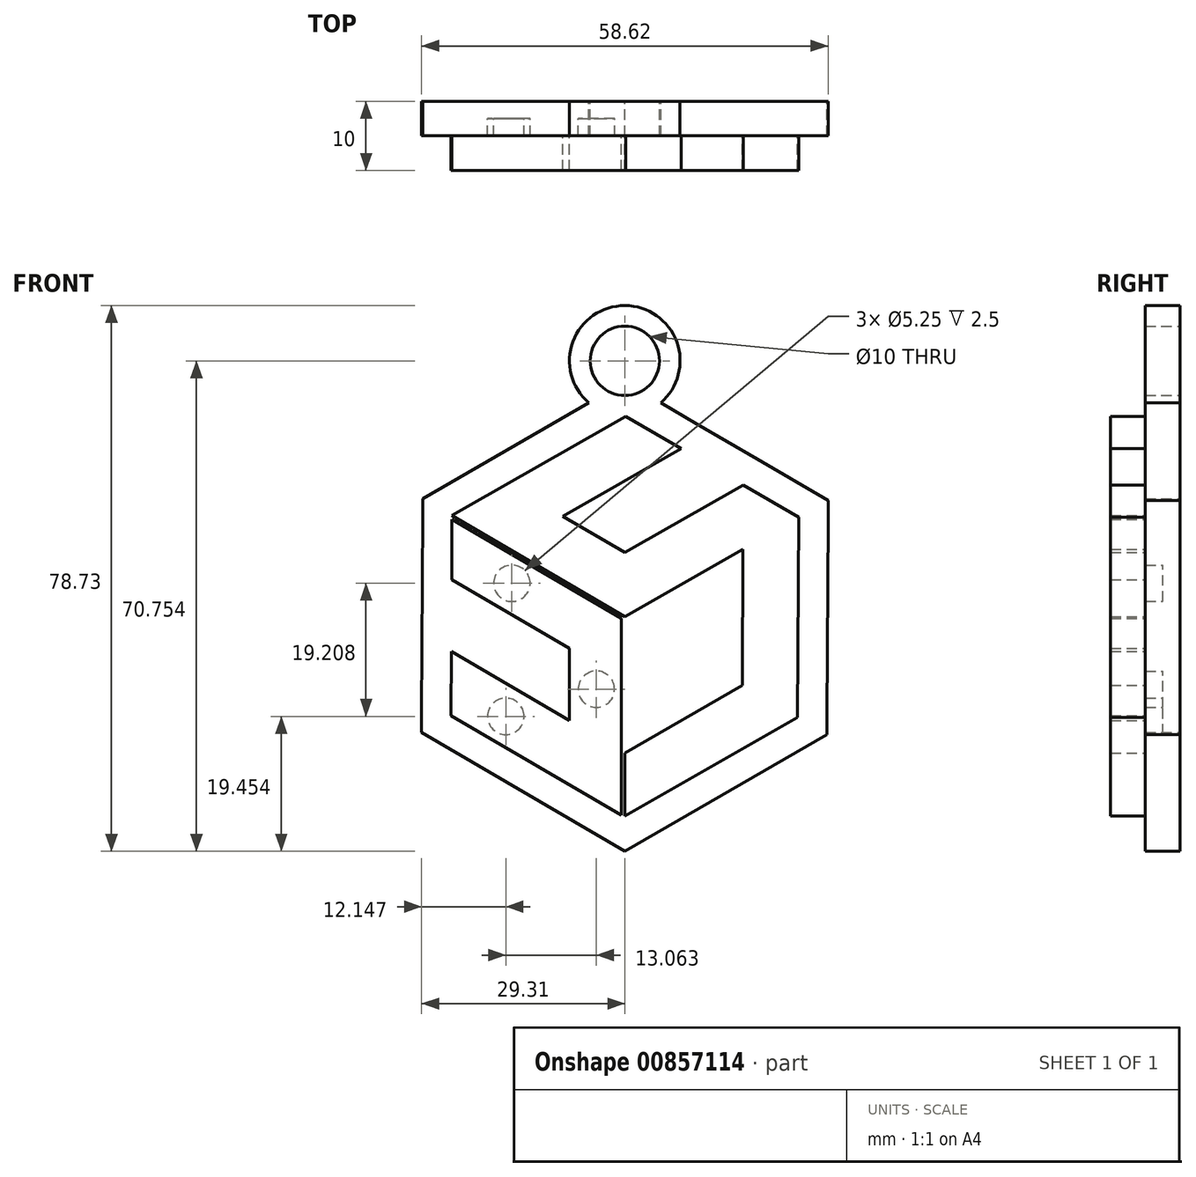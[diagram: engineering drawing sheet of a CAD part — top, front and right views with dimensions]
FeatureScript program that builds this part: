
annotation { "Feature Type Name" : "Feature", "Feature Type Description" : "" }
export const myFeature = defineFeature(function(context is Context, id is Id, definition is map)
    precondition{}
    {
        {
            var Q0;
            Q0=qCreatedBy(makeId("Front.planeOp"),FACE);
            var sketch = newSketch(context, id + "F0", { "sketchPlane" : qUnion([Q0])});
            skCircle(sketch, "E0.cCircle", {"center": v(0, 0) * mm, "radius": 25 * mm, "construction": true});
            skLineSegment(sketch, "E0.0", {"start": v(24.92, -14.56) * mm, "end": v(0, -28.78) * mm});
            skLineSegment(sketch, "E0.3", {"start": v(-24.92, 14.56) * mm, "end": v(0.15, 28.87) * mm});
            skLineSegment(sketch, "E0.5", {"start": v(25.07, 14.3) * mm, "end": v(24.92, -14.56) * mm});
            skPoint(sketch, "E0.0.midPoint", {"position": v(12.39, -21.72) * mm});
            skLineSegment(sketch, "E1.0", {"start": v(-8.93, 14.48) * mm, "end": v(8.13, 24.2) * mm});
            skLineSegment(sketch, "E2.0", {"start": v(17.1, 18.96) * mm, "end": v(0, 9.27) * mm});
            skLineSegment(sketch, "E3.0", {"start": v(-8.93, 14.48) * mm, "end": v(0, 9.27) * mm});
            skLineSegment(sketch, "E4.0", {"start": v(17.05, 9.73) * mm, "end": v(16.95, -9.9) * mm});
            skLineSegment(sketch, "E5", {"start": v(16.95, -9.9) * mm, "end": v(0, -19.69) * mm});
            skLineSegment(sketch, "E6", {"start": v(17.05, 9.73) * mm, "end": v(0, 0) * mm});
            skLineSegment(sketch, "E7", {"start": v(0, 0) * mm, "end": v(-24.92, 14.56) * mm});
            skLineSegment(sketch, "E8", {"start": v(0.15, 28.87) * mm, "end": v(8.13, 24.2) * mm});
            skLineSegment(sketch, "E9", {"start": v(17.1, 18.96) * mm, "end": v(25.07, 14.3) * mm});
            skLineSegment(sketch, "E10", {"start": v(0, -19.69) * mm, "end": v(0, -28.78) * mm});
            skLineSegment(sketch, "E11", {"start": v(0, -28.78) * mm, "end": v(0, -28.78) * mm});
            skSolve(sketch);
        }
        {
            var Q0;
            Q0 = qSketchRegion(id + "F0", true);
            extrude(context, id + "F1", {"entities" : qUnion([Q0]), "depth" : 10 * mm, "offsetDistance" : 25 * mm});
        }
        {
            var Q0;
            Q0=qCreatedBy(makeId("Front.planeOp"),FACE);
            var sketch = newSketch(context, id + "F2", { "sketchPlane" : qUnion([Q0])});
            skLineSegment(sketch, "E12.0", {"start": v(19.12, 22.7) * mm, "end": v(29.31, 16.74) * mm});
            skLineSegment(sketch, "E13.0", {"start": v(29.31, 13.92) * mm, "end": v(29.16, -14.22) * mm});
            skLineSegment(sketch, "E14.0", {"start": v(0, -33.86) * mm, "end": v(-29.31, -16.74) * mm});
            skLineSegment(sketch, "E15.0", {"start": v(-29.26, -4.91) * mm, "end": v(-29.31, -13.92) * mm});
            skLineSegment(sketch, "E16.0", {"start": v(-29.16, 14.66) * mm, "end": v(-29.21, 5.22) * mm});
            skLineSegment(sketch, "E17", {"start": v(-29.16, 17.02) * mm, "end": v(-29.16, 14.66) * mm});
            skLineSegment(sketch, "E18", {"start": v(-29.21, 5.22) * mm, "end": v(-29.26, -4.91) * mm});
            skLineSegment(sketch, "E19", {"start": v(-29.31, -13.92) * mm, "end": v(-29.31, -16.74) * mm});
            skLineSegment(sketch, "E20", {"start": v(29.16, -14.22) * mm, "end": v(29.16, -17.02) * mm});
            skLineSegment(sketch, "E21", {"start": v(10.38, 27.8) * mm, "end": v(19.12, 22.7) * mm});
            skLineSegment(sketch, "E22", {"start": v(29.31, 16.74) * mm, "end": v(29.31, 13.92) * mm});
            skLineSegment(sketch, "E23", {"start": v(-29.16, 17.02) * mm, "end": v(-6.93, 29.86) * mm});
            skLineSegment(sketch, "E24", {"start": v(0, -33.86) * mm, "end": v(29.16, -17.02) * mm});
            skLineSegment(sketch, "E25", {"start": v(6.9, 29.83) * mm, "end": v(10.38, 27.8) * mm});
            skLineSegment(sketch, "E26", {"start": v(-6.93, 29.86) * mm, "end": v(-5.2, 30.86) * mm});
            skLineSegment(sketch, "E27", {"start": v(6.9, 29.83) * mm, "end": v(5.18, 30.83) * mm});
            skPoint(sketch, "E28", {"position": v(0, 36.9) * mm});
            skArc(sketch, "E29", {"start": v(5.18, 30.83) * mm, "mid": v(0.02, 44.87) * mm, "end": v(-5.2, 30.86) * mm});
            skSolve(sketch);
        }
        {
            var Q0;
            Q0 = qSketchRegion(id + "F2", true);
            extrude(context, id + "F3", {"entities" : qUnion([Q0]), "operationType" : NewBodyOperationType.ADD, "depth" : 5 * mm, "offsetDistance" : 25 * mm});
        }
        {
            var Q0;
            Q0=qCreatedBy(makeId("Front.planeOp"),FACE);
            var sketch = newSketch(context, id + "F4", { "sketchPlane" : qUnion([Q0])});
            skLineSegment(sketch, "E30.0", {"start": v(-8, -4.6) * mm, "end": v(-24.97, 5.33) * mm});
            skLineSegment(sketch, "E31.0", {"start": v(-8, -4.6) * mm, "end": v(-8, -15.01) * mm});
            skLineSegment(sketch, "E32.0", {"start": v(-25.03, -5.07) * mm, "end": v(-8, -15.01) * mm});
            skLineSegment(sketch, "E33.0", {"start": v(-25.03, -5.07) * mm, "end": v(-25.07, -14.3) * mm});
            skLineSegment(sketch, "E34.0", {"start": v(-0.5, -19.69) * mm, "end": v(-0.5, -28.66) * mm});
            skLineSegment(sketch, "E35", {"start": v(-0.5, -0.29) * mm, "end": v(-24.93, 13.99) * mm});
            skLineSegment(sketch, "E36", {"start": v(-0.5, -0.29) * mm, "end": v(-0.5, -19.69) * mm});
            skLineSegment(sketch, "E37", {"start": v(-0.5, -28.66) * mm, "end": v(-25.07, -14.3) * mm});
            skLineSegment(sketch, "E38", {"start": v(-24.93, 13.99) * mm, "end": v(-24.97, 5.33) * mm});
            skSolve(sketch);
        }
        {
            var Q0;
            Q0=sQuery(id+"F2.wireOp",VERTEX,"E28");
            var Q1;
            Q1=makeQuery(id+"F1.opExtrude","SWEPT_BODY",BODY,{"disambiguationData":[OSD([sQuery(id+"F0.wireOp",EDGE,"E0.0"),sQuery(id+"F0.wireOp",EDGE,"E0.3"),sQuery(id+"F0.wireOp",EDGE,"E0.5"),sQuery(id+"F0.wireOp",EDGE,"E1.0"),sQuery(id+"F0.wireOp",EDGE,"E2.0"),sQuery(id+"F0.wireOp",EDGE,"E3.0"),sQuery(id+"F0.wireOp",EDGE,"E4.0"),sQuery(id+"F0.wireOp",EDGE,"E5"),sQuery(id+"F0.wireOp",EDGE,"E6"),sQuery(id+"F0.wireOp",EDGE,"E7"),sQuery(id+"F0.wireOp",EDGE,"E8"),sQuery(id+"F0.wireOp",EDGE,"E9"),sQuery(id+"F0.wireOp",EDGE,"E10")])]});
            hole(context, id + "F5", {"style" : HoleStyle.SIMPLE, "endStyle" : HoleEndStyle.THROUGH, "oppositeDirection" : true, "holeDiameter" : 10 * mm, "majorDiameter" : 5 * mm, "isTappedThrough" : true, "tappedDepth" : 12 * mm, "tapClearance" : 3, "locations" : qUnion([Q0]), "scope" : qUnion([Q1])});
        }
        {
            var Q0;
            Q0=makeQuery(id+"F3.opExtrude","CAP_FACE",FACE,{"disambiguationData":[OSD([sQuery(id+"F2.wireOp",EDGE,"E12.0"),sQuery(id+"F2.wireOp",EDGE,"E13.0"),sQuery(id+"F2.wireOp",EDGE,"E14.0"),sQuery(id+"F2.wireOp",EDGE,"E15.0"),sQuery(id+"F2.wireOp",EDGE,"E16.0"),sQuery(id+"F2.wireOp",EDGE,"E17"),sQuery(id+"F2.wireOp",EDGE,"E18"),sQuery(id+"F2.wireOp",EDGE,"E19"),sQuery(id+"F2.wireOp",EDGE,"E20"),sQuery(id+"F2.wireOp",EDGE,"E21"),sQuery(id+"F2.wireOp",EDGE,"E22"),sQuery(id+"F2.wireOp",EDGE,"E23"),sQuery(id+"F2.wireOp",EDGE,"E24"),sQuery(id+"F2.wireOp",EDGE,"E25"),sQuery(id+"F2.wireOp",EDGE,"E26"),sQuery(id+"F2.wireOp",EDGE,"E27"),sQuery(id+"F2.wireOp",EDGE,"E29")])],"isStart":false});
            cPlane(context, id + "F6", {"entities" : qUnion([Q0]), "cplaneType" : CPlaneType.OFFSET, "offset" : 0 * mm, "width" : 150 * mm, "height" : 150 * mm});
        }
        {
            var Q0;
            Q0=qCreatedBy(id+"F6.planeOp",FACE);
            var sketch = newSketch(context, id + "F7", { "sketchPlane" : qUnion([Q0])});
            skLineSegment(sketch, "E39.0.0", {"start": v(-0.5, -28.66) * mm, "end": v(-0.5, -0.29) * mm});
            skLineSegment(sketch, "E39.0.1", {"start": v(-0.5, -0.29) * mm, "end": v(-24.93, 13.99) * mm});
            skLineSegment(sketch, "E39.0.2", {"start": v(-24.93, 13.99) * mm, "end": v(-24.97, 5.33) * mm});
            skLineSegment(sketch, "E39.0.3", {"start": v(-24.97, 5.33) * mm, "end": v(-8, -4.6) * mm});
            skLineSegment(sketch, "E39.0.4", {"start": v(-8, -4.6) * mm, "end": v(-8, -15.01) * mm});
            skLineSegment(sketch, "E39.0.5", {"start": v(-8, -15.01) * mm, "end": v(-25.03, -5.07) * mm});
            skLineSegment(sketch, "E39.0.6", {"start": v(-25.03, -5.07) * mm, "end": v(-25.07, -14.3) * mm});
            skLineSegment(sketch, "E39.0.7", {"start": v(-25.07, -14.3) * mm, "end": v(-0.5, -28.66) * mm});
            skSolve(sketch);
        }
        {
            var Q0;
            Q0 = qSketchRegion(id + "F7", true);
            extrude(context, id + "F8", {"entities" : qUnion([Q0]), "depth" : 5 * mm, "offsetDistance" : 25 * mm});
        }
        {
            var Q0;
            Q0=qCreatedBy(id+"F6.planeOp",FACE);
            var sketch = newSketch(context, id + "F9", { "sketchPlane" : qUnion([Q0])});
            skCircle(sketch, "E40", {"center": v(-16.29, 4.8) * mm, "radius": 2.38 * mm});
            skCircle(sketch, "E41", {"center": v(-17.16, -14.4) * mm, "radius": 2.38 * mm});
            skCircle(sketch, "E42", {"center": v(-4.1, -10.5) * mm, "radius": 2.38 * mm});
            skSolve(sketch);
        }
        {
            var Q0;
            Q0 = qSketchRegion(id + "F9", true);
            extrude(context, id + "F10", {"entities" : qUnion([Q0]), "operationType" : NewBodyOperationType.ADD, "oppositeDirection" : true, "depth" : 2 * mm, "offsetDistance" : 25 * mm});
        }
        {
            var Q0;
            Q0=makeQuery(id+"F3.opExtrude","CAP_FACE",FACE,{"disambiguationData":[OSD([sQuery(id+"F2.wireOp",EDGE,"E12.0"),sQuery(id+"F2.wireOp",EDGE,"E13.0"),sQuery(id+"F2.wireOp",EDGE,"E14.0"),sQuery(id+"F2.wireOp",EDGE,"E15.0"),sQuery(id+"F2.wireOp",EDGE,"E16.0"),sQuery(id+"F2.wireOp",EDGE,"E17"),sQuery(id+"F2.wireOp",EDGE,"E18"),sQuery(id+"F2.wireOp",EDGE,"E19"),sQuery(id+"F2.wireOp",EDGE,"E20"),sQuery(id+"F2.wireOp",EDGE,"E21"),sQuery(id+"F2.wireOp",EDGE,"E22"),sQuery(id+"F2.wireOp",EDGE,"E23"),sQuery(id+"F2.wireOp",EDGE,"E24"),sQuery(id+"F2.wireOp",EDGE,"E25"),sQuery(id+"F2.wireOp",EDGE,"E26"),sQuery(id+"F2.wireOp",EDGE,"E27"),sQuery(id+"F2.wireOp",EDGE,"E29")])],"isStart":false});
            cPlane(context, id + "F11", {"entities" : qUnion([Q0]), "cplaneType" : CPlaneType.OFFSET, "offset" : 2.5 * mm, "oppositeDirection" : true, "width" : 150 * mm, "height" : 150 * mm});
        }
        {
            var Q0;
            Q0=qCreatedBy(id+"F11.planeOp",FACE);
            var sketch = newSketch(context, id + "F12", { "sketchPlane" : qUnion([Q0])});
            skPoint(sketch, "E43.0", {"position": v(-16.29, 4.8) * mm});
            skPoint(sketch, "E44.0", {"position": v(-17.16, -14.4) * mm});
            skPoint(sketch, "E45.0", {"position": v(-4.1, -10.5) * mm});
            skCircle(sketch, "E46", {"center": v(-16.29, 4.8) * mm, "radius": 2.62 * mm});
            skCircle(sketch, "E47", {"center": v(-4.1, -10.5) * mm, "radius": 2.62 * mm});
            skCircle(sketch, "E48", {"center": v(-17.16, -14.4) * mm, "radius": 2.62 * mm});
            skSolve(sketch);
        }
        {
            var Q0;
            Q0 = qSketchRegion(id + "F12", true);
            extrude(context, id + "F13", {"entities" : qUnion([Q0]), "operationType" : NewBodyOperationType.REMOVE, "depth" : 2.5 * mm, "offsetDistance" : 25 * mm});
        }
    });
